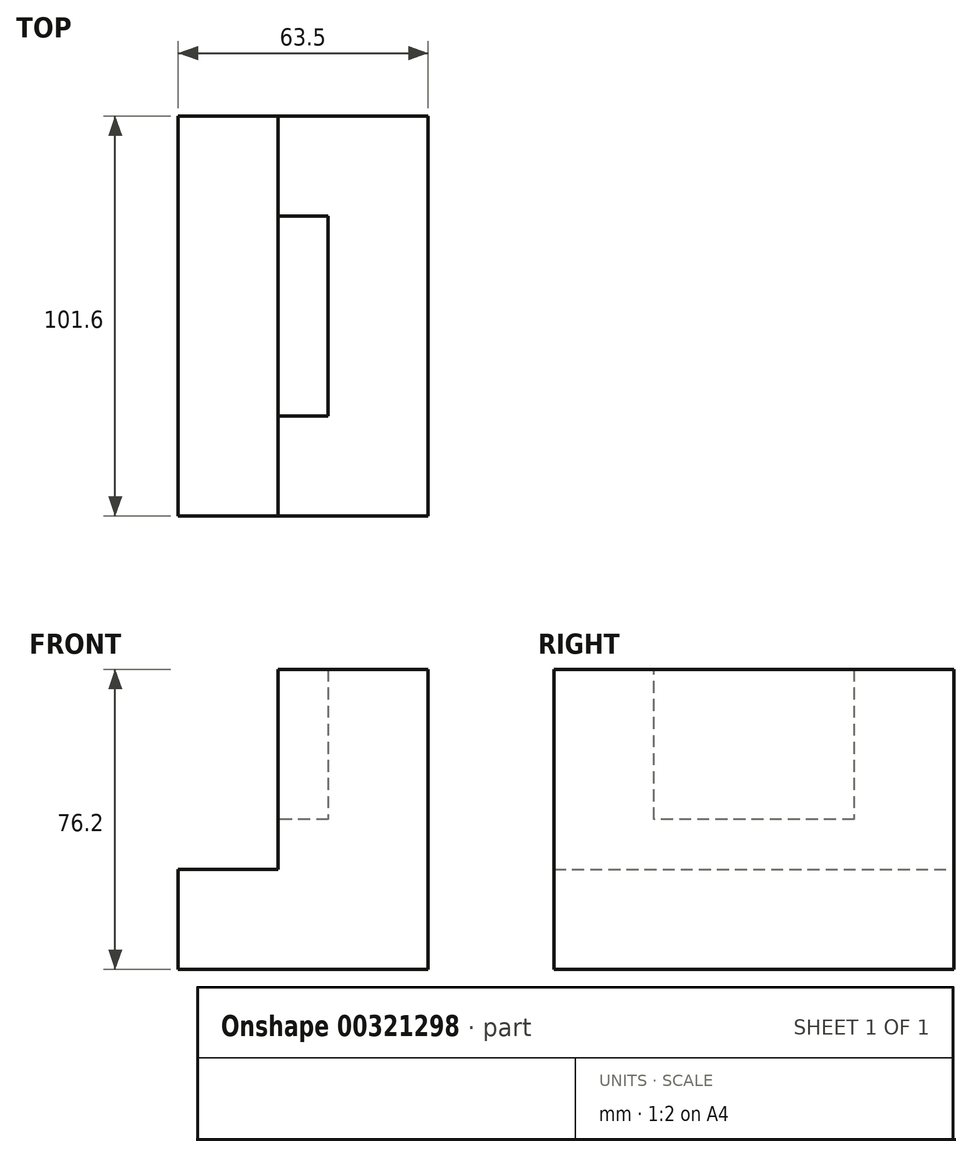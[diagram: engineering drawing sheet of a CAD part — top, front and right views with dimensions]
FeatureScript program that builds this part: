
annotation { "Feature Type Name" : "Feature", "Feature Type Description" : "" }
export const myFeature = defineFeature(function(context is Context, id is Id, definition is map)
    precondition{}
    {
        {
            var Q0;
            Q0=qCreatedBy(makeId("Front.planeOp"),FACE);
            var sketch = newSketch(context, id + "F0", { "sketchPlane" : qUnion([Q0])});
            skLineSegment(sketch, "E0", {"start": v(-68.53, -43.12) * mm, "end": v(-5.03, -43.12) * mm});
            skLineSegment(sketch, "E1", {"start": v(-5.03, -43.12) * mm, "end": v(-5.03, 33.08) * mm});
            skLineSegment(sketch, "E2", {"start": v(-5.03, 33.08) * mm, "end": v(-43.13, 33.08) * mm});
            skLineSegment(sketch, "E3", {"start": v(-68.53, -43.12) * mm, "end": v(-68.53, -17.72) * mm});
            skLineSegment(sketch, "E4", {"start": v(-68.53, -17.72) * mm, "end": v(-43.13, -17.72) * mm});
            skLineSegment(sketch, "E5", {"start": v(-43.13, 33.08) * mm, "end": v(-43.13, -17.72) * mm});
            skSolve(sketch);
        }
        {
            var Q0;
            Q0 = qSketchRegion(id + "F0", true);
            extrude(context, id + "F1", {"entities" : qUnion([Q0]), "depth" : 101.6 * mm});
        }
        {
            var Q0;
            Q0=makeQuery(id+"F1.opExtrude","SWEPT_FACE",FACE,{"disambiguationData":[OSD([sQuery(id+"F0.wireOp",EDGE,"E5")])]});
            var sketch = newSketch(context, id + "F2", { "sketchPlane" : qUnion([Q0])});
            skLineSegment(sketch, "E6", {"start": v(25.4, 33.08) * mm, "end": v(25.4, -5.02) * mm});
            skLineSegment(sketch, "E7", {"start": v(25.4, -5.02) * mm, "end": v(76.2, -5.02) * mm});
            skLineSegment(sketch, "E8", {"start": v(76.2, -5.02) * mm, "end": v(76.2, 33.08) * mm});
            skSolve(sketch);
        }
        {
            var Q0;
            Q0 = qSketchRegion(id + "F2", true);
            var Q1;
            {var subQ0=sQuery(id+"F2.wireOp",EDGE,"E6");Q1=makeQuery(id+"F2.imprint","IMPRINT",FACE,{"disambiguationData":[TD([[makeQuery(id+"F2.imprint","IMPRINT",EDGE,{"derivedFrom":subQ0}),1.0]])]});}
            extrude(context, id + "F3", {"entities" : qUnion([Q0, Q1]), "operationType" : NewBodyOperationType.REMOVE, "oppositeDirection" : true, "depth" : 12.7 * mm});
        }
    });
